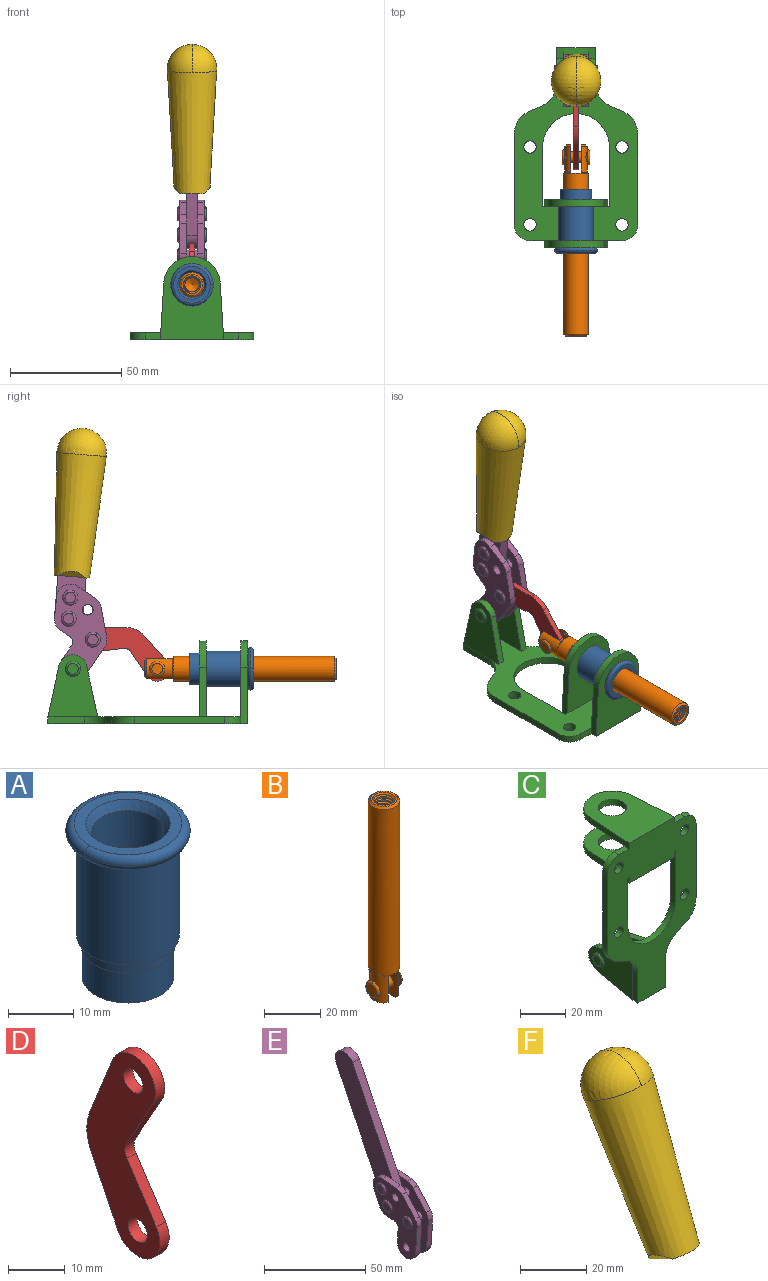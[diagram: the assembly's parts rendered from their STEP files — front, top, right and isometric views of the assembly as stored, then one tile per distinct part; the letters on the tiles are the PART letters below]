
ASSEMBLY  parts=6 mates=6
PART A: 15 faces, bbox 20.6x20.6x28.7 mm
  f0: torus R=8.26mm, axis (0,0,1), area 56.8mm2, adj f1,f10,f12
  f1: torus R=8.26mm, axis (0,0,1), area 56.8mm2, adj f0,f6,f13
  f2: cylinder r=5.59mm len=25.91mm, axis (0,0,1), area 909.6mm2, adj f3,f4
  f3: cone r=6.86mm half-angle=45deg, axis (0,0,-1), area 70.2mm2, adj f2,f14
  f4: cone r=6.47mm half-angle=30deg, axis (0,0,1), area 66.7mm2, adj f2,f13
  f5: cylinder r=7.04mm len=14.07mm, axis (0,0,1), area 252.6mm2, adj f11,f14
  f6: torus R=8.26mm, axis (0,0,1), area 56.8mm2, adj f1,f12,f13
  f7: cylinder r=7.16mm len=14.33mm, axis (0,0,1), area 91.5mm2, adj f9,f11
  f8: cylinder r=7.86mm len=18.42mm, axis (0,0,1), area 909.6mm2, adj f9,f10
  f9: plane 15.72x15.72mm, normal (0,0,-1), area 33mm2, adj f7,f8
  f10: plane 16.51x16.51mm, normal (0,0,-1), area 19.9mm2, adj f0,f8,f12
  f11: plane 14.33x14.33mm, normal (0,0,-1), area 5.7mm2, adj f5,f7
  f12: torus R=8.26mm, axis (0,0,1), area 56.8mm2, adj f0,f6,f10
  f13: plane 16.51x16.51mm, normal (0,0,1), area 82.7mm2, adj f1,f4,f6
  f14: plane 14.07x14.07mm, normal (0,0,-1), area 7.8mm2, adj f3,f5
PART B: 48 faces, bbox 12.6x11.1x86.1 mm
  f0: torus R=2.41mm, axis (-1,0,0), area 15mm2, adj f30,f32,f34
  f1: torus R=2.41mm, axis (-1,0,0), area 15mm2, adj f29,f31,f33
  f2: cylinder r=5.54mm len=72.39mm, axis (0,0,1), area 2518.5mm2, adj f3,f4,f42,f43
  f3: cone r=5.54mm half-angle=45deg, axis (0,0,1), area 7.6mm2, adj f2,f5,f41
  f4: cone r=5.54mm half-angle=45deg, axis (0,0,-1), area 34.9mm2, adj f2,f39
  f5: cylinder r=5.08mm len=11.48mm, axis (0,0,1), area 108.3mm2, adj f3,f7,f8,f41
  f6: cylinder r=2.41mm len=4.83mm, axis (-1,0,0), area 71.2mm2, adj f40,f41
  f7: cylinder r=2.41mm len=4.83mm, axis (-1,0,0), area 7.6mm2, adj f5,f34
  f8: cone r=5.08mm half-angle=45deg, axis (0,0,1), area 10.6mm2, adj f5,f37,f41
  f9: cone r=3.98mm half-angle=45deg, axis (0,0,1), area 17.6mm2, adj f27,f39,f45,f46,f47
  f10: cylinder r=2.41mm len=4.83mm, axis (-1,0,0), area 7.6mm2, adj f33,f38
  f11: cylinder r=3.2mm len=6.4mm, axis (0,0,1), area 78.4mm2, adj f12,f28,f44,f45,f47
  f12: cylinder r=3.2mm len=6.4mm, axis (0,0,1), area 10.5mm2, adj f11,f13,f45,f47
  f13: cylinder r=3.2mm len=6.4mm, axis (0,0,1), area 10.5mm2, adj f12,f14,f45,f47
  f14: cylinder r=3.2mm len=6.4mm, axis (0,0,1), area 10.5mm2, adj f13,f15,f45,f47
  f15: cylinder r=3.2mm len=6.4mm, axis (0,0,1), area 10.5mm2, adj f14,f16,f45,f47
  f16: cylinder r=3.2mm len=6.4mm, axis (0,0,1), area 10.5mm2, adj f15,f17,f45,f47
  f17: cylinder r=3.2mm len=6.4mm, axis (0,0,1), area 10.5mm2, adj f16,f18,f45,f47
  f18: cylinder r=3.2mm len=6.4mm, axis (0,0,1), area 10.5mm2, adj f17,f19,f45,f47
  f19: cylinder r=3.2mm len=6.4mm, axis (0,0,1), area 10.5mm2, adj f18,f20,f45,f47
  f20: cylinder r=3.2mm len=6.4mm, axis (0,0,1), area 10.5mm2, adj f19,f21,f45,f47
  f21: cylinder r=3.2mm len=6.4mm, axis (0,0,1), area 10.5mm2, adj f20,f22,f45,f47
  f22: cylinder r=3.2mm len=6.4mm, axis (0,0,1), area 10.5mm2, adj f21,f23,f45,f47
  f23: cylinder r=3.2mm len=6.4mm, axis (0,0,1), area 10.5mm2, adj f22,f24,f45,f47
  f24: cylinder r=3.2mm len=6.4mm, axis (0,0,1), area 10.5mm2, adj f23,f25,f45,f47
  f25: cylinder r=3.2mm len=6.4mm, axis (0,0,1), area 10.5mm2, adj f24,f26,f45,f47
  f26: cylinder r=3.2mm len=6.4mm, axis (0,0,1), area 10.5mm2, adj f25,f27,f45,f47
  f27: cylinder r=3.2mm len=6.4mm, axis (0,0,1), area 7.4mm2, adj f9,f26,f45,f47
  f28: cone r=3.2mm half-angle=60deg, axis (0,0,1), area 37.2mm2, adj f11
  f29: plane 4.83x4.83mm, normal (-1,0,0), area 18.3mm2, adj f1,f31
  f30: plane 4.83x4.83mm, normal (1,0,0), area 18.3mm2, adj f0,f32
  f31: torus R=2.41mm, axis (-1,0,0), area 15mm2, adj f1,f29,f33
  f32: torus R=2.41mm, axis (-1,0,0), area 15mm2, adj f0,f30,f34
  f33: plane 6.83x6.83mm, normal (1,0,0), area 18.3mm2, adj f1,f10,f31
  f34: plane 6.83x6.83mm, normal (-1,0,0), area 18.3mm2, adj f0,f7,f32
  f35: cone r=5.08mm half-angle=45deg, axis (0,0,1), area 10.6mm2, adj f36,f38,f40
  f36: plane 7.25x1.97mm, normal (0,0,-1), area 10mm2, adj f35,f40
  f37: plane 7.25x1.97mm, normal (0,0,-1), area 10mm2, adj f8,f41
  f38: cylinder r=5.08mm len=11.48mm, axis (0,0,1), area 108.3mm2, adj f10,f35,f40,f42
  f39: plane 9.55x9.55mm, normal (0,0,1), area 22mm2, adj f4,f9
  f40: plane 12.76x10.09mm, normal (1,0,0), area 95.7mm2, adj f6,f35,f36,f38,f42,f43
  f41: plane 12.76x10.09mm, normal (-1,0,0), area 95.7mm2, adj f3,f5,f6,f8,f37,f43
  f42: cone r=5.54mm half-angle=45deg, axis (0,0,1), area 7.6mm2, adj f2,f38,f40
  f43: plane 11.07x4.7mm, normal (0,0,-1), area 50.4mm2, adj f2,f40,f41
  f44: plane 0.89x0.62mm, normal (-1,0,0), area 0.3mm2, adj f11,f45,f46,f47
  f45: bspline ~24.8x7.63mm, area 266.6mm2, adj f9,f11,f12,f13,f14,f15,f16,f17
  f46: bspline ~24.87x7.63mm, area 73.6mm2, adj f9,f44,f45,f47
  f47: bspline ~24.98x7.63mm, area 272.5mm2, adj f9,f11,f12,f13,f14,f15,f16,f17
PART C: 55 faces, bbox 55.7x37.4x89.8 mm
  f0: torus R=2.41mm, axis (-1,0,0), area 15mm2, adj f11,f15,f25
  f1: torus R=2.41mm, axis (-1,0,0), area 15mm2, adj f10,f12,f22
  f2: cylinder r=2.78mm len=5.56mm, axis (0,-1,0), area 54.2mm2, adj f30,f54
  f3: cylinder r=14.99mm len=29.97mm, axis (0,-1,0), area 145.9mm2, adj f30,f49,f53,f54
  f4: cylinder r=2.78mm len=5.56mm, axis (0,-1,0), area 54.2mm2, adj f30,f54
  f5: cylinder r=2.78mm len=5.56mm, axis (0,-1,0), area 54.2mm2, adj f30,f54
  f6: cylinder r=2.78mm len=5.56mm, axis (0,-1,0), area 54.2mm2, adj f30,f54
  f7: cylinder r=6.35mm len=12.7mm, axis (0,0,1), area 123.6mm2, adj f27,f51
  f8: cylinder r=6.35mm len=12.7mm, axis (0,0,-1), area 124.7mm2, adj f21,f35
  f9: cylinder r=2.41mm len=11.18mm, axis (-1,0,0), area 169.4mm2, adj f16,f19
  f10: plane 4.83x4.83mm, normal (1,0,0), area 18.3mm2, adj f1,f12
  f11: plane 4.83x4.83mm, normal (-1,0,0), area 18.3mm2, adj f0,f15
  f12: torus R=2.41mm, axis (-1,0,0), area 15mm2, adj f1,f10,f22
  f13: cylinder r=6.35mm len=12.41mm, axis (1,0,0), area 53.4mm2, adj f18,f19,f22,f23
  f14: cylinder r=6.35mm len=12.41mm, axis (-1,0,0), area 53.4mm2, adj f16,f17,f24,f25
  f15: torus R=2.41mm, axis (-1,0,0), area 15mm2, adj f0,f11,f25
  f16: plane 27.86x22.35mm, normal (1,0,0), area 425.4mm2, adj f9,f14,f17,f24,f30
  f17: plane 22.86x4.97mm, normal (0,0.21,0.98), area 72.5mm2, adj f14,f16,f25,f30
  f18: plane 22.86x4.97mm, normal (0,0.21,0.98), area 72.5mm2, adj f13,f19,f22,f30
  f19: plane 27.86x22.35mm, normal (-1,0,0), area 425.4mm2, adj f9,f13,f18,f23,f30
  f20: cylinder r=12.7mm len=25.35mm, axis (0,0,-1), area 119.8mm2, adj f21,f34,f35,f36
  f21: plane 34.21x28.07mm, normal (0,0,-1), area 702.4mm2, adj f8,f20,f30,f34,f36
  f22: plane 27.96x22.45mm, normal (1,0,0), area 407.2mm2, adj f1,f12,f13,f18,f23,f30,f42,f43
  f23: plane 22.86x4.97mm, normal (0,0.21,-0.98), area 72.5mm2, adj f13,f19,f22,f44
  f24: plane 22.86x4.97mm, normal (0,0.21,-0.98), area 72.5mm2, adj f14,f16,f25,f44
  f25: plane 27.86x22.35mm, normal (-1,0,0), area 407.1mm2, adj f0,f14,f15,f17,f24,f30,f45,f46
  f26: plane 3.1x0.95mm, normal (0,0,-1), area 2.7mm2, adj f30,f49,f50,f54
  f27: plane 34.21x28.07mm, normal (0,0,1), area 702.4mm2, adj f7,f28,f30,f50,f52
  f28: cylinder r=12.7mm len=25.35mm, axis (0,0,1), area 118.8mm2, adj f27,f50,f51,f52
  f29: plane 3.1x0.95mm, normal (0,0,-1), area 2.7mm2, adj f30,f52,f53,f54
  f30: plane 86.54x55.63mm, normal (0,1,0), area 2362.9mm2, adj f2,f3,f4,f5,f6,f16,f17,f18
  f31: plane 40.56x3.1mm, normal (-1,0,0), area 125.7mm2, adj f30,f32,f48,f54
  f32: cylinder r=7.11mm len=7.11mm, axis (0,-1,0), area 34.6mm2, adj f30,f31,f33,f54
  f33: plane 6.67x3.1mm, normal (0,0,1), area 20.4mm2, adj f30,f32,f34,f54
  f34: plane 25.39x3.13mm, normal (-1,0.06,0), area 79.5mm2, adj f20,f21,f33,f35,f54
  f35: plane 37.31x28.45mm, normal (0,0,1), area 789.9mm2, adj f8,f20,f34,f36,f54
  f36: plane 25.39x3.13mm, normal (1,0.06,0), area 79.5mm2, adj f20,f21,f35,f37,f54
  f37: plane 6.67x3.1mm, normal (0,0,1), area 20.4mm2, adj f30,f36,f38,f54
  f38: cylinder r=7.11mm len=7.11mm, axis (0,-1,0), area 34.6mm2, adj f30,f37,f39,f54
  f39: plane 40.56x3.1mm, normal (1,0,0), area 125.7mm2, adj f30,f38,f40,f54
  f40: cylinder r=11.18mm len=10.16mm, axis (0,-1,0), area 39.5mm2, adj f30,f39,f41,f54
  f41: plane 6.09x3.1mm, normal (0.42,0,-0.91), area 20.8mm2, adj f30,f40,f42,f54
  f42: cylinder r=11.18mm len=9.41mm, axis (0,-1,0), area 37.2mm2, adj f22,f30,f41,f43,f54
  f43: plane 16.5x3.1mm, normal (1,0,0), area 51.1mm2, adj f22,f42,f44,f54
  f44: plane 17.37x3.1mm, normal (0,0,-1), area 53.8mm2, adj f23,f24,f30,f43,f45,f54
  f45: plane 16.5x3.1mm, normal (-1,0,0), area 51.1mm2, adj f25,f44,f46,f54
  f46: cylinder r=11.18mm len=9.41mm, axis (0,-1,0), area 37.2mm2, adj f25,f30,f45,f47,f54
  f47: plane 6.09x3.1mm, normal (-0.42,0,-0.91), area 20.8mm2, adj f30,f46,f48,f54
  f48: cylinder r=11.18mm len=10.16mm, axis (0,-1,0), area 39.5mm2, adj f30,f31,f47,f54
  f49: plane 26.54x3.1mm, normal (-1,0,0), area 82.3mm2, adj f3,f26,f30,f54
  f50: plane 25.39x3.1mm, normal (1,0.06,0), area 78.8mm2, adj f26,f27,f28,f51,f54
  f51: plane 37.31x28.45mm, normal (0,0,-1), area 789.9mm2, adj f7,f28,f50,f52,f54
  f52: plane 25.39x3.1mm, normal (-1,0.06,0), area 78.8mm2, adj f27,f28,f29,f51,f54
  f53: plane 26.54x3.1mm, normal (1,0,0), area 82.3mm2, adj f3,f29,f30,f54
  f54: plane 89.66x55.63mm, normal (0,-1,0), area 2678.5mm2, adj f2,f3,f4,f5,f6,f26,f29,f31
PART D: 12 faces, bbox 2.3x18.2x42.8 mm
  f0: cylinder r=2.4mm len=4.8mm, axis (1,0,0), area 34.9mm2, adj f4,f11
  f1: cylinder r=10.41mm len=8.47mm, axis (1,0,0), area 20.2mm2, adj f4,f9,f10,f11
  f2: cylinder r=3.05mm len=3.16mm, axis (1,0,0), area 7.7mm2, adj f4,f6,f7,f11
  f3: cylinder r=2.4mm len=4.8mm, axis (1,0,0), area 34.9mm2, adj f4,f11
  f4: plane 42.81x18.23mm, normal (-1,0,0), area 414.1mm2, adj f0,f1,f2,f3,f5,f6,f7,f8
  f5: cylinder r=5.54mm len=10.67mm, axis (1,0,0), area 41.8mm2, adj f4,f6,f10,f11
  f6: plane 11.66x6.53mm, normal (0,-0.87,-0.49), area 30.9mm2, adj f2,f4,f5,f11
  f7: plane 11.17x7.33mm, normal (0,-0.84,0.55), area 30.9mm2, adj f2,f4,f8,f11
  f8: cylinder r=5.54mm len=10.51mm, axis (1,0,0), area 41.8mm2, adj f4,f7,f9,f11
  f9: plane 13.67x6.67mm, normal (0,0.9,-0.44), area 35.1mm2, adj f1,f4,f8,f11
  f10: plane 14.1x5.7mm, normal (0,0.93,0.37), area 35.1mm2, adj f1,f4,f5,f11
  f11: plane 42.81x18.23mm, normal (1,0,0), area 414.1mm2, adj f0,f1,f2,f3,f5,f6,f7,f8
PART E: 59 faces, bbox 12.9x60.2x99.6 mm
  f0: torus R=2.39mm, axis (-1,0,0), area 14.9mm2, adj f20,f43,f51
  f1: torus R=2.39mm, axis (-1,0,0), area 14.9mm2, adj f19,f42,f51
  f2: torus R=2.39mm, axis (-1,0,0), area 14.9mm2, adj f18,f35,f51
  f3: torus R=2.39mm, axis (-1,0,0), area 14.9mm2, adj f14,f17,f23
  f4: torus R=2.39mm, axis (-1,0,0), area 14.9mm2, adj f13,f16,f23
  f5: torus R=2.39mm, axis (-1,0,0), area 14.9mm2, adj f12,f15,f23
  f6: cylinder r=2.39mm len=4.78mm, axis (1,0,0), area 46.5mm2, adj f48,f50,f51
  f7: cylinder r=2.39mm len=4.78mm, axis (1,0,0), area 46.5mm2, adj f50,f51
  f8: cylinder r=6.35mm len=12.68mm, axis (1,0,0), area 61.8mm2, adj f38,f39,f50,f51
  f9: cylinder r=2.39mm len=4.78mm, axis (-1,0,0), area 70.5mm2, adj f46,f50
  f10: cylinder r=2.39mm len=4.78mm, axis (-1,0,0), area 46.5mm2, adj f23,f45,f46
  f11: cylinder r=2.39mm len=4.78mm, axis (-1,0,0), area 46.5mm2, adj f23,f46
  f12: plane 4.78x4.78mm, normal (1,0,0), area 17.9mm2, adj f5,f15
  f13: plane 4.78x4.78mm, normal (1,0,0), area 17.9mm2, adj f4,f16
  f14: plane 4.78x4.78mm, normal (1,0,0), area 17.9mm2, adj f3,f17
  f15: torus R=2.39mm, axis (-1,0,0), area 14.9mm2, adj f5,f12,f23
  f16: torus R=2.39mm, axis (-1,0,0), area 14.9mm2, adj f4,f13,f23
  f17: torus R=2.39mm, axis (-1,0,0), area 14.9mm2, adj f3,f14,f23
  f18: plane 4.78x4.78mm, normal (-1,0,0), area 17.9mm2, adj f2,f35
  f19: plane 4.78x4.78mm, normal (-1,0,0), area 17.9mm2, adj f1,f42
  f20: plane 4.78x4.78mm, normal (-1,0,0), area 17.9mm2, adj f0,f43
  f21: plane 2.26x0.2mm, normal (1,0,0), area 0.2mm2, adj f31,f44
  f22: plane 2.26x0.2mm, normal (-1,0,0), area 0.2mm2, adj f41,f44
  f23: plane 39.37x30.77mm, normal (1,0,0), area 565.5mm2, adj f3,f4,f5,f10,f11,f15,f16,f17
  f24: cylinder r=6.1mm len=4.15mm, axis (-1,0,0), area 14.7mm2, adj f23,f25,f32,f46
  f25: plane 10.25x9.01mm, normal (0,-0.75,0.66), area 42.3mm2, adj f23,f24,f26,f46
  f26: cylinder r=6.35mm len=4.64mm, axis (-1,0,0), area 15.6mm2, adj f23,f25,f27,f46
  f27: plane 15.84x3.1mm, normal (0,-1,-0.07), area 49.2mm2, adj f23,f26,f28,f46
  f28: cylinder r=6.35mm len=12.68mm, axis (-1,0,0), area 61.8mm2, adj f23,f27,f29,f46
  f29: plane 8.11x3.1mm, normal (0,1,0.07), area 25.2mm2, adj f23,f28,f30,f46
  f30: cylinder r=3.05mm len=3.25mm, axis (-1,0,0), area 14.8mm2, adj f23,f29,f31,f46
  f31: plane 5.99x3.1mm, normal (0,0.07,-1), area 18.6mm2, adj f21,f23,f30,f44,f46
  f32: plane 9.5x3.1mm, normal (0,-0.07,1), area 29.5mm2, adj f23,f24,f33,f46,f47
  f33: cylinder r=6.1mm len=8.63mm, axis (-1,0,0), area 39.1mm2, adj f23,f32,f34,f47
  f34: plane 8.65x3.96mm, normal (0,0.91,-0.42), area 29.5mm2, adj f23,f33,f44,f47
  f35: torus R=2.39mm, axis (-1,0,0), area 14.9mm2, adj f2,f18,f51
  f36: plane 10.25x9.01mm, normal (0,-0.75,0.66), area 42.3mm2, adj f37,f49,f50,f51
  f37: cylinder r=6.35mm len=4.64mm, axis (1,0,0), area 15.6mm2, adj f36,f38,f50,f51
  f38: plane 15.84x3.1mm, normal (0,-1,-0.07), area 49.2mm2, adj f8,f37,f50,f51
  f39: plane 8.11x3.1mm, normal (0,1,0.07), area 25.2mm2, adj f8,f40,f50,f51
  f40: cylinder r=3.05mm len=3.25mm, axis (1,0,0), area 14.8mm2, adj f39,f41,f50,f51
  f41: plane 5.99x3.1mm, normal (0,0.07,-1), area 18.6mm2, adj f22,f40,f44,f50,f51
  f42: torus R=2.39mm, axis (-1,0,0), area 14.9mm2, adj f1,f19,f51
  f43: torus R=2.39mm, axis (-1,0,0), area 14.9mm2, adj f0,f20,f51
  f44: cylinder r=6.35mm len=12.12mm, axis (-1,0,0), area 128.9mm2, adj f21,f22,f23,f31,f34,f41,f46,f47
  f45: plane 2.65x1.35mm, normal (1,0,0), area 1mm2, adj f10,f55
  f46: plane 39.08x20.42mm, normal (-1,0,0), area 412.5mm2, adj f9,f10,f11,f24,f25,f26,f27,f28
  f47: plane 77.62x39.82mm, normal (1,0,0), area 850mm2, adj f32,f33,f34,f44,f53,f54,f55
  f48: plane 2.65x1.35mm, normal (-1,0,0), area 1mm2, adj f6,f55
  f49: cylinder r=6.1mm len=4.15mm, axis (1,0,0), area 14.7mm2, adj f36,f50,f51,f56
  f50: plane 39.08x20.42mm, normal (1,0,0), area 412.5mm2, adj f6,f7,f8,f9,f36,f37,f38,f39
  f51: plane 39.37x30.77mm, normal (-1,0,0), area 565.5mm2, adj f0,f1,f2,f6,f7,f8,f35,f36
  f52: plane 8.65x3.96mm, normal (0,0.91,-0.42), area 29.5mm2, adj f44,f51,f57,f58
  f53: plane 68.49x33.4mm, normal (0,0.9,-0.44), area 358.1mm2, adj f44,f47,f54,f58
  f54: cylinder r=6.35mm len=12.06mm, axis (1,0,0), area 93.7mm2, adj f47,f53,f55,f58
  f55: plane 68.49x33.4mm, normal (0,-0.9,0.44), area 358.1mm2, adj f44,f45,f46,f47,f48,f50,f54,f58
  f56: plane 9.5x3.1mm, normal (0,-0.07,1), area 29.5mm2, adj f49,f50,f51,f57,f58
  f57: cylinder r=6.1mm len=8.63mm, axis (1,0,0), area 39.1mm2, adj f51,f52,f56,f58
  f58: plane 77.62x39.82mm, normal (-1,0,0), area 850mm2, adj f44,f52,f53,f54,f55,f56,f57
PART F: 11 faces, bbox 22.3x42.6x64.5 mm
  f0: sphere r=11.13mm, area 411.4mm2, adj f1,f8
  f1: cone r=11.11mm half-angle=3.3deg, axis (0,0.44,0.9), area 3251.8mm2, adj f0,f7,f8,f9,f10
  f2: cylinder r=6.16mm len=11.7mm, axis (1,0,0), area 89.5mm2, adj f3,f4,f5,f6
  f3: plane 60.23x36.75mm, normal (-1,0,0), area 763.6mm2, adj f2,f4,f6,f10
  f4: plane 51.37x25.05mm, normal (0,0.9,-0.44), area 264.2mm2, adj f2,f3,f5,f10
  f5: plane 60.23x36.75mm, normal (1,0,0), area 763.6mm2, adj f2,f4,f6,f10
  f6: plane 51.37x25.05mm, normal (0,-0.9,0.44), area 264.2mm2, adj f2,f3,f5,f10
  f7: plane 9.95x5.95mm, normal (0.71,-0.31,-0.64), area 25.8mm2, adj f1,f10
  f8: sphere r=11.13mm, area 411.4mm2, adj f0,f1
  f9: plane 9.95x5.95mm, normal (-0.71,-0.31,-0.64), area 25.8mm2, adj f1,f10
  f10: plane 14.27x11.38mm, normal (0,-0.44,-0.9), area 106.7mm2, adj f1,f3,f4,f5,f6,f7,f9
PLACE A rot(axis=(1,0,0),90deg) t=(0,9.43,0)mm
PLACE B rot(axis=(1,0,0),90deg) t=(0,19.07,0)mm
PLACE C rot(axis=(1,0,0),90deg) t=(0,9.43,0)mm fixed
PLACE D rot(axis=(1,0,0),116.3deg) t=(0,28.38,9.41)mm
PLACE E rot(axis=(1,0,0),30.5deg) t=(0,4.02,39.76)mm
PLACE F rot(axis=(1,0,0),30.5deg) t=(0.01,4.02,39.76)mm
MATE revolute D.f5 <-> B.f6  axis (1,0,0) through (0,3.59,24.61)mm
MATE revolute E.f7 <-> C.f0  axis (1,0,0) through (0,41.52,24.61)mm
MATE fastened E.f54 <-> F.f2  axis (1,0,0) through (0,37.39,123.02)mm
MATE revolute D.f3 <-> E.f4  axis (1,0,0) through (0,32.52,37.69)mm
MATE slider B.f2 <-> C.f7  axis (0,-1,0) through (0,-39.71,24.61)mm
MATE fastened A.f0 <-> C.f7  axis (0,1,0) through (0,-36.96,24.61)mm
